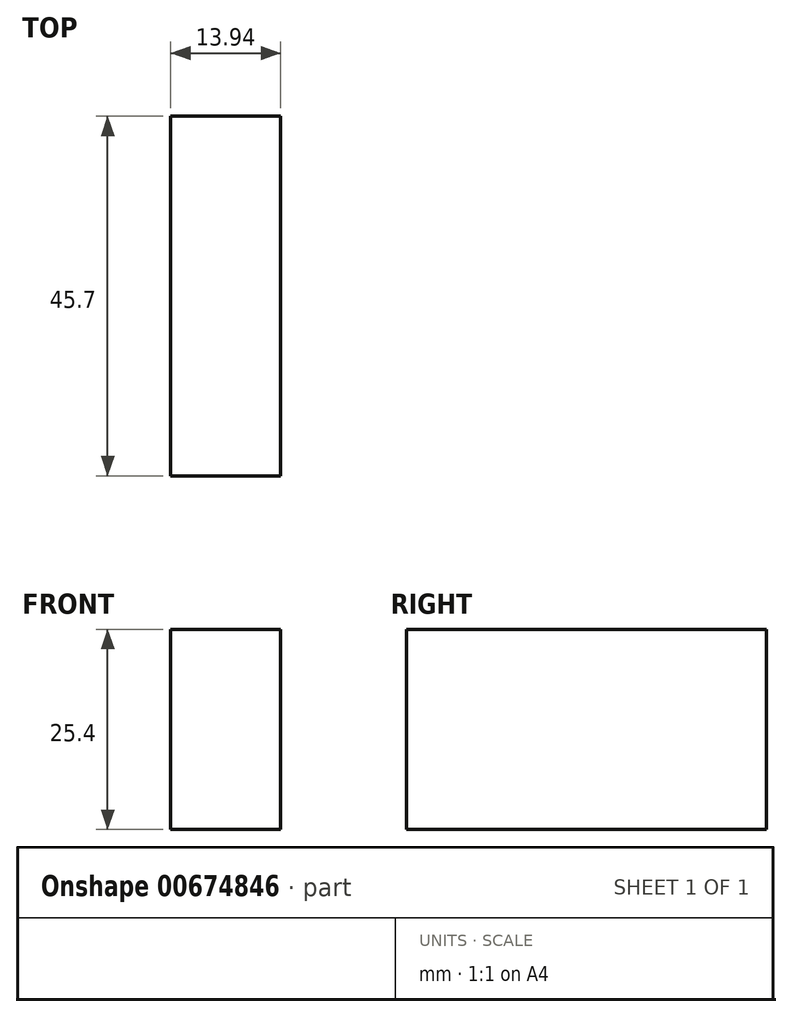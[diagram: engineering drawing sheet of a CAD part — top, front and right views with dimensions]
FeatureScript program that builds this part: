
annotation { "Feature Type Name" : "Feature", "Feature Type Description" : "" }
export const myFeature = defineFeature(function(context is Context, id is Id, definition is map)
    precondition{}
    {
        {
            var Q0;
            Q0=qCreatedBy(makeId("Top.planeOp"),FACE);
            var sketch = newSketch(context, id + "F0", { "sketchPlane" : qUnion([Q0])});
            skLineSegment(sketch, "E0.bottom", {"start": v(-6.97, 22.85) * mm, "end": v(6.97, 22.85) * mm});
            skLineSegment(sketch, "E0.top", {"start": v(-6.97, -22.85) * mm, "end": v(6.97, -22.85) * mm});
            skLineSegment(sketch, "E0.left", {"start": v(-6.97, 22.85) * mm, "end": v(-6.97, -22.85) * mm});
            skLineSegment(sketch, "E0.right", {"start": v(6.97, 22.85) * mm, "end": v(6.97, -22.85) * mm});
            skPoint(sketch, "E0.middle", {"position": v(0, 0) * mm});
            skSolve(sketch);
        }
        {
            var Q0;
            Q0=makeQuery(id+"F0.imprint","IMPRINT",FACE,{"disambiguationData":[TD([[makeQuery(id+"F0.imprint","IMPRINT",EDGE,{"derivedFrom":sQuery(id+"F0.wireOp",EDGE,"E0.bottom")}),-1.0]])]});
            extrude(context, id + "F1", {"entities" : qUnion([Q0]), "depth" : 25.4 * mm, "offsetDistance" : 25.4 * mm});
        }
    });
